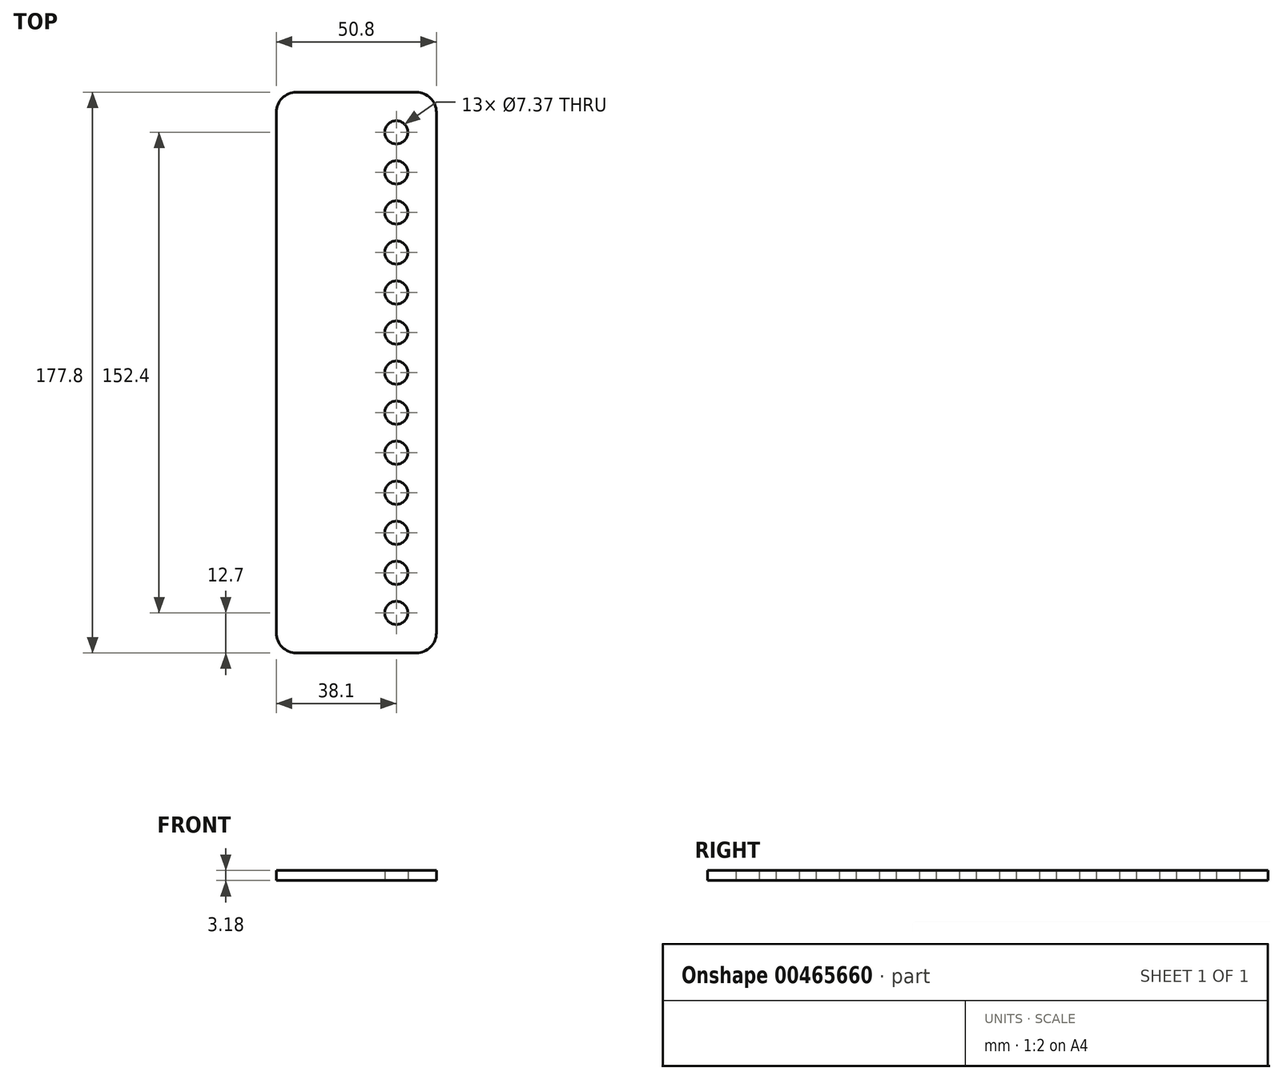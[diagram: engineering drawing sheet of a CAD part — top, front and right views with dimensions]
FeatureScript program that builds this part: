
annotation { "Feature Type Name" : "Feature", "Feature Type Description" : "" }
export const myFeature = defineFeature(function(context is Context, id is Id, definition is map)
    precondition{}
    {
        {
            var Q0;
            Q0=qCreatedBy(makeId("Top.planeOp"),FACE);
            var sketch = newSketch(context, id + "F0", { "sketchPlane" : qUnion([Q0])});
            skLineSegment(sketch, "E0.bottom", {"start": v(6.35, 0) * mm, "end": v(44.45, 0) * mm});
            skLineSegment(sketch, "E0.top", {"start": v(6.35, 177.8) * mm, "end": v(44.45, 177.8) * mm});
            skLineSegment(sketch, "E0.left", {"start": v(0, 6.35) * mm, "end": v(0, 171.45) * mm});
            skLineSegment(sketch, "E0.right", {"start": v(50.8, 6.35) * mm, "end": v(50.8, 171.45) * mm});
            skCircle(sketch, "E1", {"center": v(38.1, 12.7) * mm, "radius": 3.68 * mm});
            skCircle(sketch, "E2.0.1.0", {"center": v(38.1, 25.4) * mm, "radius": 3.68 * mm});
            skCircle(sketch, "E2.0.2.0", {"center": v(38.1, 38.1) * mm, "radius": 3.68 * mm});
            skCircle(sketch, "E2.0.3.0", {"center": v(38.1, 50.8) * mm, "radius": 3.68 * mm});
            skCircle(sketch, "E2.0.4.0", {"center": v(38.1, 63.5) * mm, "radius": 3.68 * mm});
            skCircle(sketch, "E2.0.5.0", {"center": v(38.1, 76.2) * mm, "radius": 3.68 * mm});
            skCircle(sketch, "E2.0.6.0", {"center": v(38.1, 88.9) * mm, "radius": 3.68 * mm});
            skCircle(sketch, "E2.0.7.0", {"center": v(38.1, 101.6) * mm, "radius": 3.68 * mm});
            skCircle(sketch, "E2.0.8.0", {"center": v(38.1, 114.3) * mm, "radius": 3.68 * mm});
            skCircle(sketch, "E2.0.9.0", {"center": v(38.1, 127) * mm, "radius": 3.68 * mm});
            skCircle(sketch, "E2.0.10.0", {"center": v(38.1, 139.7) * mm, "radius": 3.68 * mm});
            skCircle(sketch, "E2.0.11.0", {"center": v(38.1, 152.4) * mm, "radius": 3.68 * mm});
            skCircle(sketch, "E2.0.12.0", {"center": v(38.1, 165.1) * mm, "radius": 3.68 * mm});
            skLineSegment(sketch, "E2.direction1", {"start": v(38.1, 12.7) * mm, "end": v(41.46, 12.7) * mm, "construction": true});
            skLineSegment(sketch, "E2.direction2", {"start": v(38.1, 12.7) * mm, "end": v(38.1, 25.4) * mm, "construction": true});
            skPoint(sketch, "E3.visualSharp", {"position": v(0, 177.8) * mm});
            skArc(sketch, "E3.filletArc", {"start": v(6.35, 177.8) * mm, "mid": v(1.86, 175.94) * mm, "end": v(0, 171.45) * mm});
            skPoint(sketch, "E4.visualSharp", {"position": v(50.8, 177.8) * mm});
            skArc(sketch, "E4.filletArc", {"start": v(50.8, 171.45) * mm, "mid": v(48.94, 175.94) * mm, "end": v(44.45, 177.8) * mm});
            skPoint(sketch, "E5.visualSharp", {"position": v(0, 0) * mm});
            skArc(sketch, "E5.filletArc", {"start": v(0, 6.35) * mm, "mid": v(1.86, 1.86) * mm, "end": v(6.35, 0) * mm});
            skPoint(sketch, "E6.visualSharp", {"position": v(50.8, 0) * mm});
            skArc(sketch, "E6.filletArc", {"start": v(44.45, 0) * mm, "mid": v(48.94, 1.86) * mm, "end": v(50.8, 6.35) * mm});
            skSolve(sketch);
        }
        {
            var Q0;
            Q0=qSketchRegion(id+"F0",true);
            extrude(context, id + "F1", {"entities" : qUnion([Q0]), "depth" : 3.17 * mm});
        }
    });
